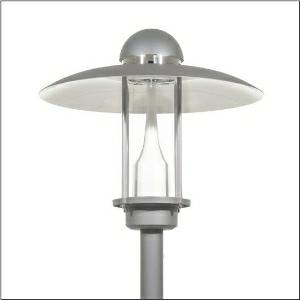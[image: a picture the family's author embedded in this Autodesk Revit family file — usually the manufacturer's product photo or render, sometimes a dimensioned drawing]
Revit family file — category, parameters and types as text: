
# Revit family: city-light_elegance_iq___st1_2a_5xa5265af14h_1cc4
name_source: partatom
category: Lighting Fixtures
units: mm (PartAtom-declared; Revit-internal decimal feet)

## family parameters
Cut with Voids When Loaded = No
Host = Face
Light Source = No
Part Type = Normal
Room Calculation Point = No
Round Connector Dimension = Use Diameter
Shared = No

## types (1)
- --- (1 x LED, 1470 lm, 12.9 W, 2200K)
    Apparent Load = 13 VA
    CIE Flux Codes = 22 62 94 98 100
    Color Rendering = 70
    Color Temperature = 2200K
    Default Elevation = 1800 mm
    Description = City-Light Elegance iQ, mast luminaire, Module 540 iQ-SR, primary light control with 3 zone facetted reflector, of plastic, silver coated, highly specular, structured, primary optical cover: cover, of PMMA, transparent, light distribution: ST1.2a, light emission: direct distribution, primary light characteristic: asymmetric, installation type: post-top, LED, High Power LED, rated luminous flux: 1.470lm, luminous efficacy: 114lm/W, light colour: 722, colour temperature: 2200K, control gear: iQ Street-Remote, control: pre-setting: logarithmic dimming characteristic, Street-Remote, Auto-Match, Temp-Guard, Lumen-Switch, Night-Set, Smart-Wire, Light-Fading, Desk-Remote (wireless, voltage-free reading and setting of iQ features in the workshop via application-optimized NFC function/RFID function), optimised constant luminous flux control (CLO 2.0), with terminal, 6-pole, max. 2.5mm², mains connection: 230..240V, AC, 50/60Hz, start of lifetime: 13W, end of service life: 13W, reduction: 6W, luminaire housing, upper part, of aluminium, coated, Siteco® metallic grey (DB 702S), diameter: 750mm, height: 675mm, spigot size: d x l = 76 x 70mm (post-top) | with reducer (optional accessory) 60 x 70mm, mounting height: 3..5m, post-top mast mounting element, of diecast aluminium, coated, Siteco® metallic grey (DB 702S), Module 540 iQ-SR, traffic white (RAL 9016), equipment: standard, protection rating (complete): IP65, insulation class (complete): insulation class II (safety insulation), certification: CE, ENEC, VDE, packaging unit: 1 piece

Light Distribution: ST1.2a
    Height = 675 mm
    Lamp = 1 x LED
    Lamp Light Flux = 1470 lm
    Lamp Power = 12.9 W
    Lamp count = 1
    Length = 750 mm
    Luminous efficacy = 114 lm/W
    Manufacturer = Siteco
    ModVariant = No
    Model = 5XA5265AF14H
    Number of Poles = 1
    OnlyDefault = Yes
    Power Factor = 1
    Product Name = City-Light Elegance iQ | ST1.2a
    Product group = mast luminaire | pylon top
    ProductGroupID = 6100
    Protection Class = Protection class II
    Protection Degree = IP 65
    RLX_Detail_Level = 1
    RLX_Emergency_Light_Flux = 0 lm
    RLX_Emergency_Type = 0
    RLX_Emergency_Type_DB = No
    RlxData = <blob elided: 99925 chars, md5=b463fac3>
    Socket = socket
    Standby Power = 0 W
    System Light Flux = 1470 lm
    System Power = 13 W
    Type Comments = factory setting: luminous flux: 100 % | dim-lin: 254 | 516 mA
    Type Image = l_1006912.jpg
    URL = http://relux.com
    VarID = @adj_181353
    Voltage = 0 V
    Weight = 0.00 kg
    Width = 0 mm  [stored 0 ft]

note: [stored X ft] marks values corroborated as IEEE doubles in the binary element streams (Revit-internal decimal feet)

## geometry (parser evidence)
native form markers: Blend x4, Sweep x12
no freeform markers — native parametric forms only
